# Revit family: Plumbing_Other-Plumbing_Menzies-Metal_Blue-Drain-Seal (7)
name_source: partatom
category: Pipe Fittings
revit_build: Autodesk Revit 2018 (Build: 20170223_1515(x64)
units: mm (PartAtom-declared; Revit-internal decimal feet)

## family parameters
Always vertical = No
Cut with Voids When Loaded = No
OmniClass Number = 23.60.30.11.14
OmniClass Title = Pipework Fittings
Part Type = Transition
Round Connector Dimension = Use Diameter
Shared = No
Work Plane-Based = No

## types (4) — shared parameters
Assembly Code = D2040200
Description = Menzies Blue Drain Seal™
Edition number = 1
Manufacturer = Menzies Metal Products
Product Guid = f62e8464-96eb-4267-9b67-e3f2fa2fb2a5
Product Material = Plastic - Menzies Metal Products - Nylon
Product data url = https://www.bimobject.com
Required Tools = Screwdriver for Blue Drain seal is required to install product; https://www.menzies-metal.com
Seal Material = Rubber - Menzies Metal Products - EPDM
URL = https://www.menzies-metal.com

## per-type parameters (varying)
| type | Model | Nominal Diameter 1 | Nominal Diameter 2 | SCH40 Pipe ID Range | SCH80 Pipe ID Range | Weight |
| 3" | 300-3130 | 2.75 " | 3 " | 2.87 - 3.40 in | 2.82 - 3.40 in | 0.56 lbf |
| 4" | 300-3135 | 3.75 " | 4 " | 3.85 - 4.40 in | 3.75 - 4.40 in | 0.98 lbf |
| 5" | 300-3140 | 4.75 " | 5 " | 4.84 - 5.40 in | 4.73 - 5.40 in | 1.05 lbf |
| 6" | 300-3145 | 5.75 " | 6 " | 5.82 - 6.40 in | 5.76 - 6.40 in | 1.20 lbf |

## geometry (parser evidence)
native form markers: Sweep x4
no freeform markers — native parametric forms only
